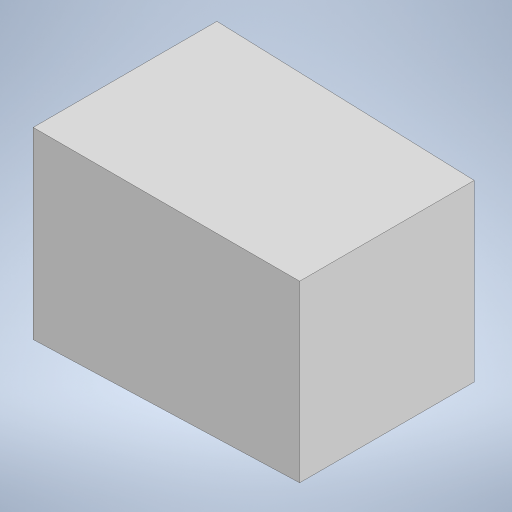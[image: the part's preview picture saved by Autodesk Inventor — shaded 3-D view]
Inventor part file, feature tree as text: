
AUTODESK INVENTOR PART (.ipt)
format: ipt  version: 2023 (Build 270158000, 158)  size: 233,984 bytes
history: native  units: in
note: dims shown in document units (in); Inventor stores cm internally (conversion verified against a paired STEP export)
features: extrude x1, draft x1
ambient origin geometry x8: Origin, YZ Plane, XZ Plane, XY Plane, X Axis, Y Axis, Z Axis, Center Point
bodies: Solid1 (feature_tree)
feature tree (2):
  extrude  "Extrusion1"  TaperAngle=0.0deg  [1 undecoded]
  draft  "FaceDraft1"
note: 1 required parameter value undecoded (feature->parameter linkage not recoverable at this tier; creation-order binding heuristic only, values carry confidence <= 0.55)
